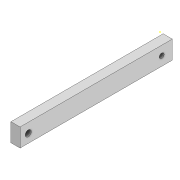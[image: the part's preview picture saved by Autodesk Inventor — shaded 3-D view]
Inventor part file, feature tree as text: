
AUTODESK INVENTOR PART (.ipt)
format: ipt  version: 2021 (Build 250183000, 183)  size: 87,552 bytes
history: native  units: in
note: dims shown in document units (in); Inventor stores cm internally (conversion verified against a paired STEP export)
features: sketch x4, extrude x3
ambient origin geometry x8: Origin, YZ Plane, XZ Plane, XY Plane, X Axis, Y Axis, Z Axis, Center Point
bodies: Solid1 (feature_tree)
feature tree (7):
  sketch  "Sketch1"  dims[d0=0.5906in d1=1.1811in]
  extrude  "Extrusion1"  Depth=1.1811in
  extrude  "Extrusion2"  Depth=9.8425in
  extrude  "Extrusion3"  Depth=0.3937in
  sketch  "Sketch2"  dims[d2=9.8425in d3=0.0in d4=0.315in]
  sketch  "Sketch3"  dims[d5=0.315in d6=0.0in d7=0.3937in]
  sketch  "Sketch4"  dims[d8=0.0in d9=0.0in]
